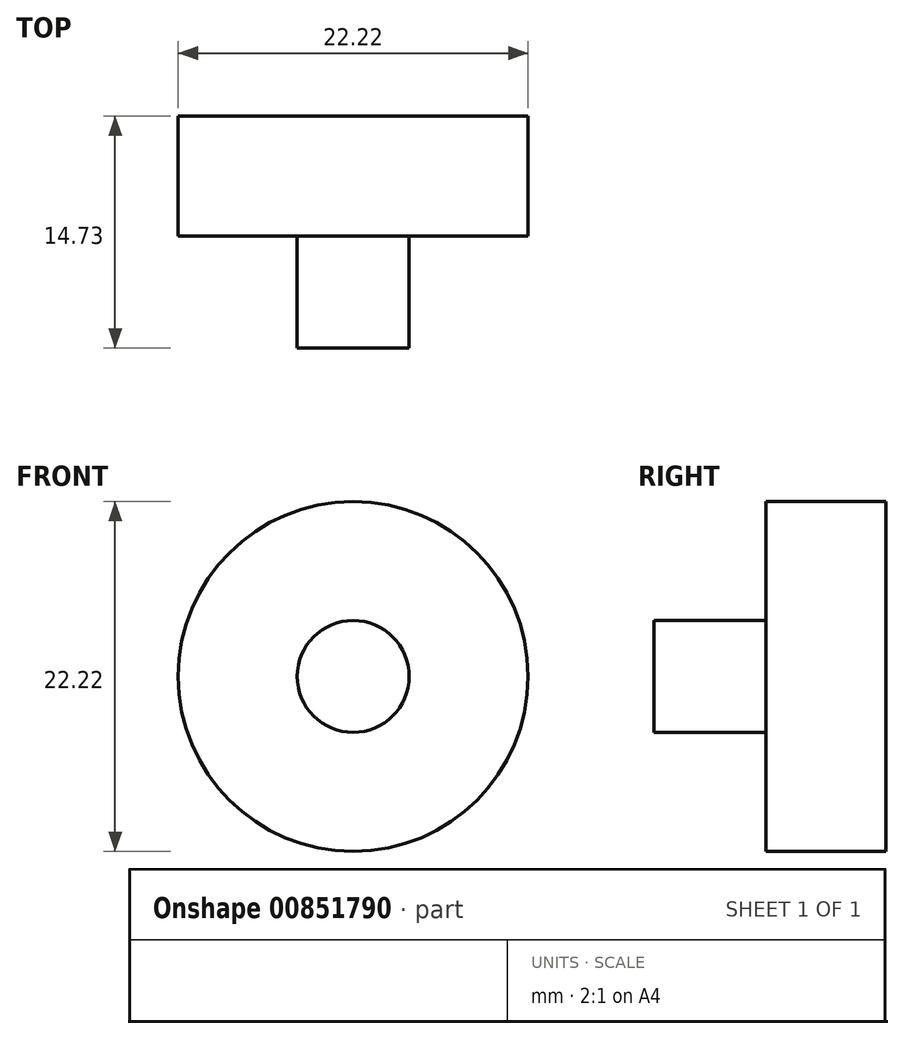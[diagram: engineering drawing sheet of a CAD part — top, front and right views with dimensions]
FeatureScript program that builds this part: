
annotation { "Feature Type Name" : "Feature", "Feature Type Description" : "" }
export const myFeature = defineFeature(function(context is Context, id is Id, definition is map)
    precondition{}
    {
        {
            var Q0;
            Q0=qCreatedBy(makeId("Front.planeOp"),FACE);
            var sketch = newSketch(context, id + "F0", { "sketchPlane" : qUnion([Q0])});
            skCircle(sketch, "E0", {"center": v(0, 0) * mm, "radius": 11.11 * mm});
            skSolve(sketch);
        }
        {
            var Q0;
            Q0 = qSketchRegion(id + "F0", true);
            extrude(context, id + "F1", {"entities" : qUnion([Q0]), "depth" : 7.62 * mm, "offsetDistance" : 25.4 * mm});
        }
        {
            var Q0;
            Q0=makeQuery(id+"F1.opExtrude","CAP_FACE",FACE,{"disambiguationData":[OSD([sQuery(id+"F0.wireOp",EDGE,"E0")])],"isStart":false});
            var sketch = newSketch(context, id + "F2", { "sketchPlane" : qUnion([Q0])});
            skCircle(sketch, "E1", {"center": v(0, 0) * mm, "radius": 3.56 * mm});
            skSolve(sketch);
        }
        {
            var Q0;
            Q0=makeQuery(id+"F2.imprint","IMPRINT",FACE,{"disambiguationData":[TD([[makeQuery(id+"F2.imprint","IMPRINT",EDGE,{"derivedFrom":sQuery(id+"F2.wireOp",EDGE,"E1")}),1.0]])]});
            var Q1;
            Q1=sQuery(id+"F2.wireOp",EDGE,"E1");
            extrude(context, id + "F3", {"entities" : qUnion([Q0]), "operationType" : NewBodyOperationType.ADD, "surfaceEntities" : qUnion([Q1]), "depth" : 7.11 * mm, "offsetDistance" : 25.4 * mm});
        }
    });
